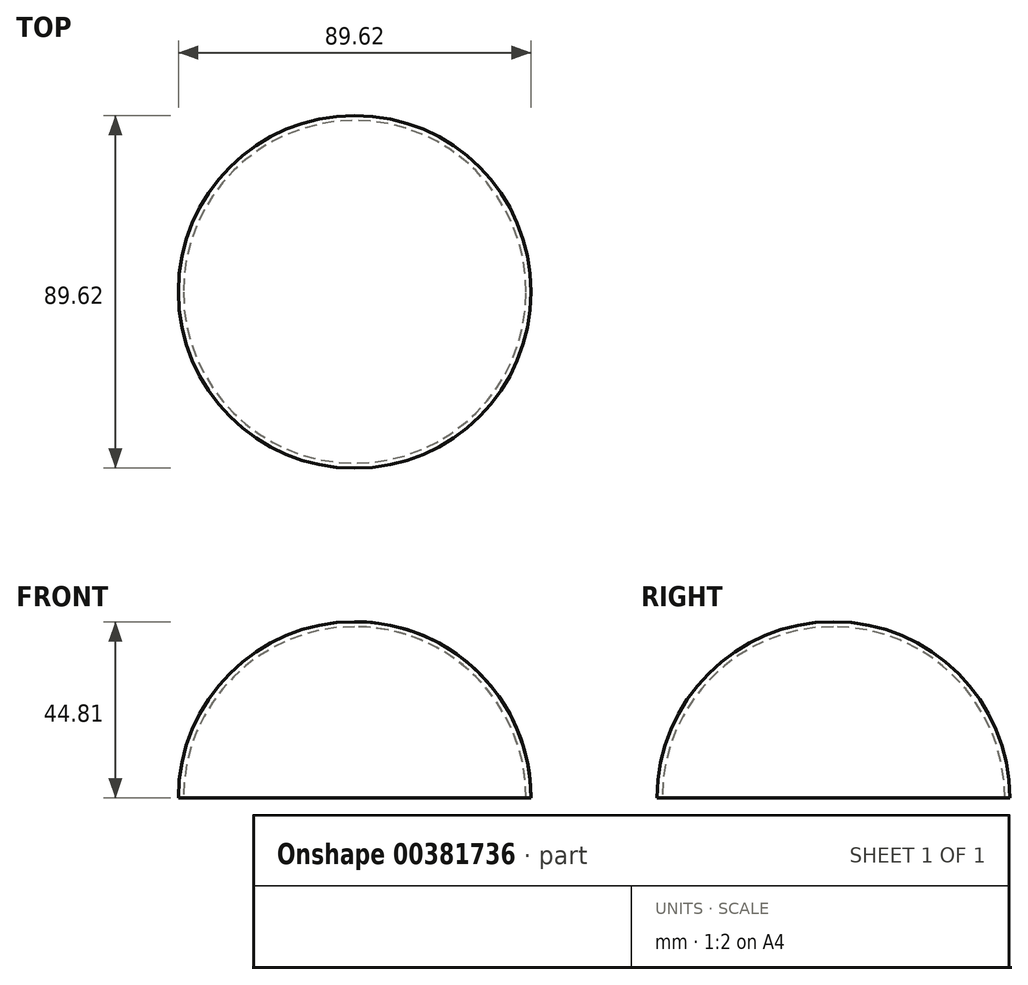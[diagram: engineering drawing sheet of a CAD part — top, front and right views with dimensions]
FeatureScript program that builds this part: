
annotation { "Feature Type Name" : "Feature", "Feature Type Description" : "" }
export const myFeature = defineFeature(function(context is Context, id is Id, definition is map)
    precondition{}
    {
        {
            var Q0;
            Q0=qCreatedBy(makeId("Front.planeOp"),FACE);
            var sketch = newSketch(context, id + "F0", { "sketchPlane" : qUnion([Q0])});
            skLineSegment(sketch, "E0", {"start": v(0, 58.86) * mm, "end": v(0, -56.01) * mm, "construction": true});
            skArc(sketch, "E1", {"start": v(-44.8, 0) * mm, "mid": v(-31.69, 31.69) * mm, "end": v(0, 44.8) * mm});
            skLineSegment(sketch, "E2", {"start": v(-44.8, 0) * mm, "end": v(0, 0) * mm});
            skLineSegment(sketch, "E3", {"start": v(0, 0) * mm, "end": v(0, 44.8) * mm});
            skSolve(sketch);
        }
        {
            var Q0;
            Q0=qSketchRegion(id+"F0",true);
            var Q1;
            Q1=sQuery(id+"F0.wireOp",EDGE,"E0");
            revolve(context, id + "F1", {"entities" : qUnion([Q0]), "axis" : qUnion([Q1]), "revolveType" : RevolveType.FULL});
        }
        {
            var Q0;
            Q0=makeQuery(id+"F1.opRevolve","SWEPT_FACE",FACE,{"disambiguationData":[OSD([sQuery(id+"F0.wireOp",EDGE,"E2")])]});
            shell(context, id + "F2", {"entities" : qUnion([Q0]), "thickness" : 1.27 * mm});
        }
    });
